# Revit family: SIMES_S.3384W_Nanoled Stainless steel Walkover
name_source: partatom
category: Lighting Fixtures
revit_build: Autodesk Revit 2016 (Build: 20150714_1515(x64)
units: mm (PartAtom-declared; Revit-internal decimal feet)

## family parameters
Cut with Voids When Loaded = No
Host = Face
Light Source = Yes
OmniClass Number = 23.80.70.14
OmniClass Title = Luminaries for External Lighting
Part Type = Normal
Room Calculation Point = No
Round Connector Dimension = Use Diameter
Shared = No

## types (1)
- SIMES_S.3384W_Nanoled Stainless steel Walkover
    Approval mark = CE
    Assembly Code = D5020
    Color Filter = 16777215
    Color Rendering Index = CRI 90
    Colour Temperature = 3000
    Control Gear = none
    Default Elevation = 1219 mm
    Description = NANOLED WALK-OVER ROUND 60mm
Art. S.3384W.19
MODULES LED 3000K  24V 2W CRI 90
Rated luminaire luminous flux: 66lm
Rated input power: 2.2W
Luminaire efficacy: 30lm/W
Without trasformer
CE

PRODUCT TYPE
Inground walk over fitting. Recessing depth 125 mm. IP rating IP 67
MATERIAL CHARACTERISTICS
Body made of AISI 316L monoblock stainless steel. Absence of screws (the luminaire is fixed to the recessing box with  OR rings). Recessing box in polypropylene. Mechanical resistance of diffusor IK 09 Maximum load capacity 500 Kg
LIGHTING PERFORMANCE
Toughened trasparent or acid-etched glass. Lamp  fixed position. LOR -- 
LOW SURFACE TEMPERATURE
Surface temperature of glass 40°C (Ta 25°C)
WIRING
Luminaire hard wired with neoprene cable 5m with cable gland. Isolation: CLASS III . Available colours: Stainless steel (cod.19). Weight: 0.8 Kg Glow Wire test: 750°C L.E.D circuit included. 
This luminaire contains built-in LED modules with energy class: A, A+, A++. In case of damage or malfunction please contact the manufacturer to receive additional instructions on how to replace and relative spare parts to order. The LED modules cannot be handled in the luminaire by the end user (Regulation UE 874/2012).
LED circuit boards are engineered accordingly to actual Lumen Maintenance regulation (LM80) and Technical Memorandum (TM21) where uniformity and quality of light is 50.000 hours referred to L70  B20 Ta 25°C.Lifecycle refers to LED circuit boards only, all others components of the luminaire are excluded.
    Dimming Lamp Color Temperature Shift = <None>
    IFC Classification = Light Fixture
    IK Rating = IK 09
    Lamp = LED
    Lamp Light Flux = 110
    Lamp Power = 2
    Lamp count = 1
    Last Update = 02/08/2018 10:41:33
    Lifetime = 50000 L70 B20 Ta 25°C
    Light Output Ratio = 100
    Luminous efficacy = 30
    Manufacturer = SIMES
    Masterformat 2014 Code = 26 56 00
    Masterformat 2014 Description = Exterior Lighting
    Model = S.3384W
    Mounting Place = Floor
    Mounting Type = Recessed
    NBS Reference Code = 49
    NBS Reference Description = Luminaries And Lamps
    OmniClass Code = 23-35 47 11
    OmniClass Description = Lighting Fixture
    Photometric Web File = S3384W.ies
    Product Group = floor-recessed luminaires
    Product Name = Nanoled Stainless steel Walkover
    Protection Class = Safety extra-low voltage
    Protection Degree = IP 67
    System Light Flux = 66
    System Power = 2,20000004768372
    Tilt Angle = 90.00°
    Type Comments = SIMES S.p.A. - All rights reserved
    Type Image = nanoled60_tondo_trasp2018.jpg
    UNSPSC Code = 3911
    URL = http://www.simes.it
    Uniclass 1.4 Code = YJ73
    Uniclass 1.4 Description = Luminaries and lamps
    Uniclass 2.0 Code = PR-49
    Uniclass 2.0 Description = Luminaries and lamps
    Uniclass 2015 Code = EF_70_80
    Uniclass 2015 Name = Lighting
    Uniformat II Code = D5020
    Uniformat II Description = Lighting & Branch Wiring
    Voltage = 24V
    Wattage Comments = 1.25W
